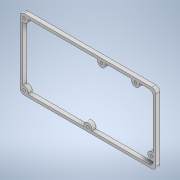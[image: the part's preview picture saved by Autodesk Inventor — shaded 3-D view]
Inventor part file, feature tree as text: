
AUTODESK INVENTOR PART (.ipt)
format: ipt  version: 2021 (Build 250183000, 183)  size: 181,248 bytes
history: native  units: mm
features: sketch x3, extrude x2, fillet x1, hole x1
ambient origin geometry x8: Origin, YZ Plane, XZ Plane, XY Plane, X Axis, Y Axis, Z Axis, Center Point
bodies: Solid1 (feature_tree)
feature tree (7):
  extrude  "Extrusion1"  Depth=52.0mm
  fillet  "Fillet1"  Radius=2.0mm
  extrude  "Extrusion2"  Depth=2.0mm
  hole  "Hole1"  [1 undecoded]
  sketch  "Sketch1"  dims[d0=100.0mm d1=52.0mm d2=2.0mm]
  sketch  "Sketch2"  dims[d3=2.0mm d4=2.0mm]
  sketch  "Sketch3"  dims[d5=2.0mm d6=3.0mm d7=0.0mm d8=3.0mm d9=3.0mm d10=3.0mm d11=3.0mm d12=50.0mm d13=8.0mm d14=97.0mm d15=3.0mm d16=49.0mm d17=60.0mm d18=49.0mm d19=85.0mm d20=49.0mm d21=6.0mm d22=6.0mm d23=6.0mm d24=6.0mm d25=6.0mm d26=3.0mm d27=0.0mm d28=2.0mm d29=6.0mm d30=4.0mm d31=2.0mm d32=90.0deg d33=4.0mm d34=20.594885mm]
note: 1 required parameter value undecoded (feature->parameter linkage not recoverable at this tier; creation-order binding heuristic only, values carry confidence <= 0.55)
